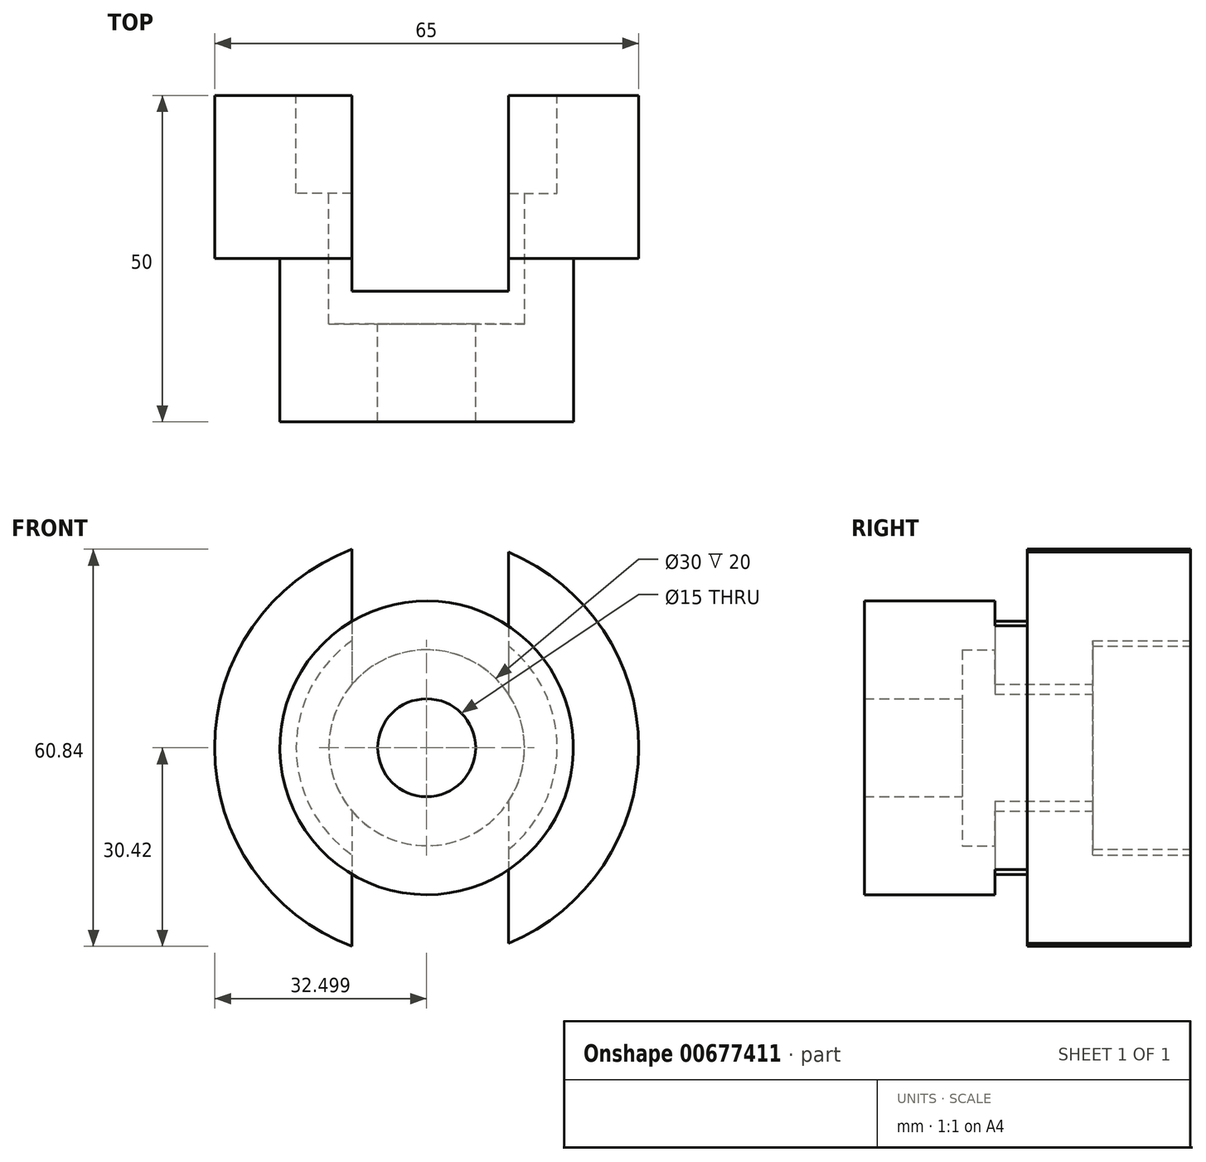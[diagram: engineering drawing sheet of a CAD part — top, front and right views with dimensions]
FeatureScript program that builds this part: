
annotation { "Feature Type Name" : "Feature", "Feature Type Description" : "" }
export const myFeature = defineFeature(function(context is Context, id is Id, definition is map)
    precondition{}
    {
        {
            var Q0;
            Q0=qCreatedBy(makeId("Front.planeOp"),FACE);
            var sketch = newSketch(context, id + "F0", { "sketchPlane" : qUnion([Q0])});
            skCircle(sketch, "E0", {"center": v(-32.57, 33.2) * mm, "radius": 32.5 * mm});
            skSolve(sketch);
        }
        {
            var Q0;
            Q0 = qSketchRegion(id + "F0", true);
            extrude(context, id + "F1", {"entities" : qUnion([Q0]), "depth" : 25 * mm, "offsetDistance" : 25 * mm});
        }
        {
            var Q0;
            Q0=makeQuery(id+"F1.opExtrude","CAP_FACE",FACE,{"disambiguationData":[OSD([sQuery(id+"F0.wireOp",EDGE,"E0")])],"isStart":false});
            var sketch = newSketch(context, id + "F2", { "sketchPlane" : qUnion([Q0])});
            skCircle(sketch, "E1", {"center": v(-32.57, 33.2) * mm, "radius": 22.5 * mm});
            skSolve(sketch);
        }
        {
            var Q0;
            Q0=makeQuery(id+"F2.imprint","IMPRINT",FACE,{"disambiguationData":[TD([[makeQuery(id+"F2.imprint","IMPRINT",EDGE,{"derivedFrom":sQuery(id+"F2.wireOp",EDGE,"E1")}),1.0]])]});
            extrude(context, id + "F3", {"entities" : qUnion([Q0]), "operationType" : NewBodyOperationType.ADD, "depth" : 25 * mm, "offsetDistance" : 25 * mm});
        }
        {
            var Q0;
            Q0=makeQuery(id+"F1.opExtrude","CAP_FACE",FACE,{"disambiguationData":[OSD([sQuery(id+"F0.wireOp",EDGE,"E0")])],"isStart":true});
            var sketch = newSketch(context, id + "F4", { "sketchPlane" : qUnion([Q0])});
            skCircle(sketch, "E2", {"center": v(32.57, 33.2) * mm, "radius": 20 * mm});
            skSolve(sketch);
        }
        {
            var Q0;
            Q0 = qSketchRegion(id + "F4", true);
            extrude(context, id + "F5", {"entities" : qUnion([Q0]), "operationType" : NewBodyOperationType.REMOVE, "oppositeDirection" : true, "depth" : 15 * mm, "offsetDistance" : 25 * mm});
        }
        {
            var Q0;
            Q0=makeQuery(id+"F5.boolean.opBoolean","COPY",FACE,{"derivedFrom":makeQuery(id+"F5.opExtrude","CAP_FACE",FACE,{"disambiguationData":[OSD([sQuery(id+"F4.wireOp",EDGE,"E2")])],"isStart":false})});
            var sketch = newSketch(context, id + "F6", { "sketchPlane" : qUnion([Q0])});
            skCircle(sketch, "E3", {"center": v(32.57, 33.2) * mm, "radius": 15 * mm});
            skSolve(sketch);
        }
        {
            var Q0;
            Q0=makeQuery(id+"F6.imprint","IMPRINT",FACE,{"disambiguationData":[TD([[makeQuery(id+"F6.imprint","IMPRINT",EDGE,{"derivedFrom":sQuery(id+"F6.wireOp",EDGE,"E3")}),1.0]])]});
            extrude(context, id + "F7", {"entities" : qUnion([Q0]), "operationType" : NewBodyOperationType.REMOVE, "oppositeDirection" : true, "depth" : 20 * mm, "offsetDistance" : 25 * mm});
        }
        {
            var Q0;
            Q0=makeQuery(id+"F7.boolean.opBoolean","COPY",FACE,{"derivedFrom":makeQuery(id+"F7.opExtrude","CAP_FACE",FACE,{"disambiguationData":[OSD([sQuery(id+"F6.wireOp",EDGE,"E3")])],"isStart":false})});
            var sketch = newSketch(context, id + "F8", { "sketchPlane" : qUnion([Q0])});
            skCircle(sketch, "E4", {"center": v(32.57, 33.2) * mm, "radius": 7.5 * mm});
            skSolve(sketch);
        }
        {
            var Q0;
            Q0=qCreatedBy(makeId("Top.planeOp"),FACE);
            var sketch = newSketch(context, id + "F9", { "sketchPlane" : qUnion([Q0])});
            skLineSegment(sketch, "E5.bottom", {"start": v(-44, 0) * mm, "end": v(-20, 0) * mm});
            skLineSegment(sketch, "E5.top", {"start": v(-44, -30) * mm, "end": v(-20, -30) * mm});
            skLineSegment(sketch, "E5.left", {"start": v(-44, 0) * mm, "end": v(-44, -30) * mm});
            skLineSegment(sketch, "E5.right", {"start": v(-20, 0) * mm, "end": v(-20, -30) * mm});
            skSolve(sketch);
        }
        {
            var Q0;
            Q0 = qSketchRegion(id + "F9", true);
            extrude(context, id + "F10", {"entities" : qUnion([Q0]), "operationType" : NewBodyOperationType.REMOVE, "depth" : 100 * mm, "offsetDistance" : 25 * mm});
        }
        {
            var Q0;
            {var subQ0=sQuery(id+"F0.wireOp",EDGE,"E0");Q0=makeQuery(id+"F10.boolean.opBoolean","SPLIT",FACE,{"disambiguationData":[TD([makeQuery(id+"F10.opExtrude","SWEPT_FACE",FACE,{"disambiguationData":[OSD([sQuery(id+"F9.wireOp",EDGE,"E5.left")])]})])],"derivedFrom":makeQuery(id+"F1.opExtrude","CAP_FACE",FACE,{"disambiguationData":[OSD([subQ0])],"isStart":true})});}
            var sketch = newSketch(context, id + "F11", { "sketchPlane" : qUnion([Q0])});
            skSolve(sketch);
        }
        {
            var Q0;
            Q0 = qSketchRegion(id + "F11", true);
            var Q1;
            Q1=makeQuery(id+"F8.imprint","IMPRINT",FACE,{"disambiguationData":[TD([[makeQuery(id+"F8.imprint","IMPRINT",EDGE,{"derivedFrom":sQuery(id+"F8.wireOp",EDGE,"E4")}),1.0]])]});
            extrude(context, id + "F12", {"entities" : qUnion([Q0, Q1]), "operationType" : NewBodyOperationType.REMOVE, "oppositeDirection" : true, "depth" : 25 * mm, "offsetDistance" : 25 * mm});
        }
    });
